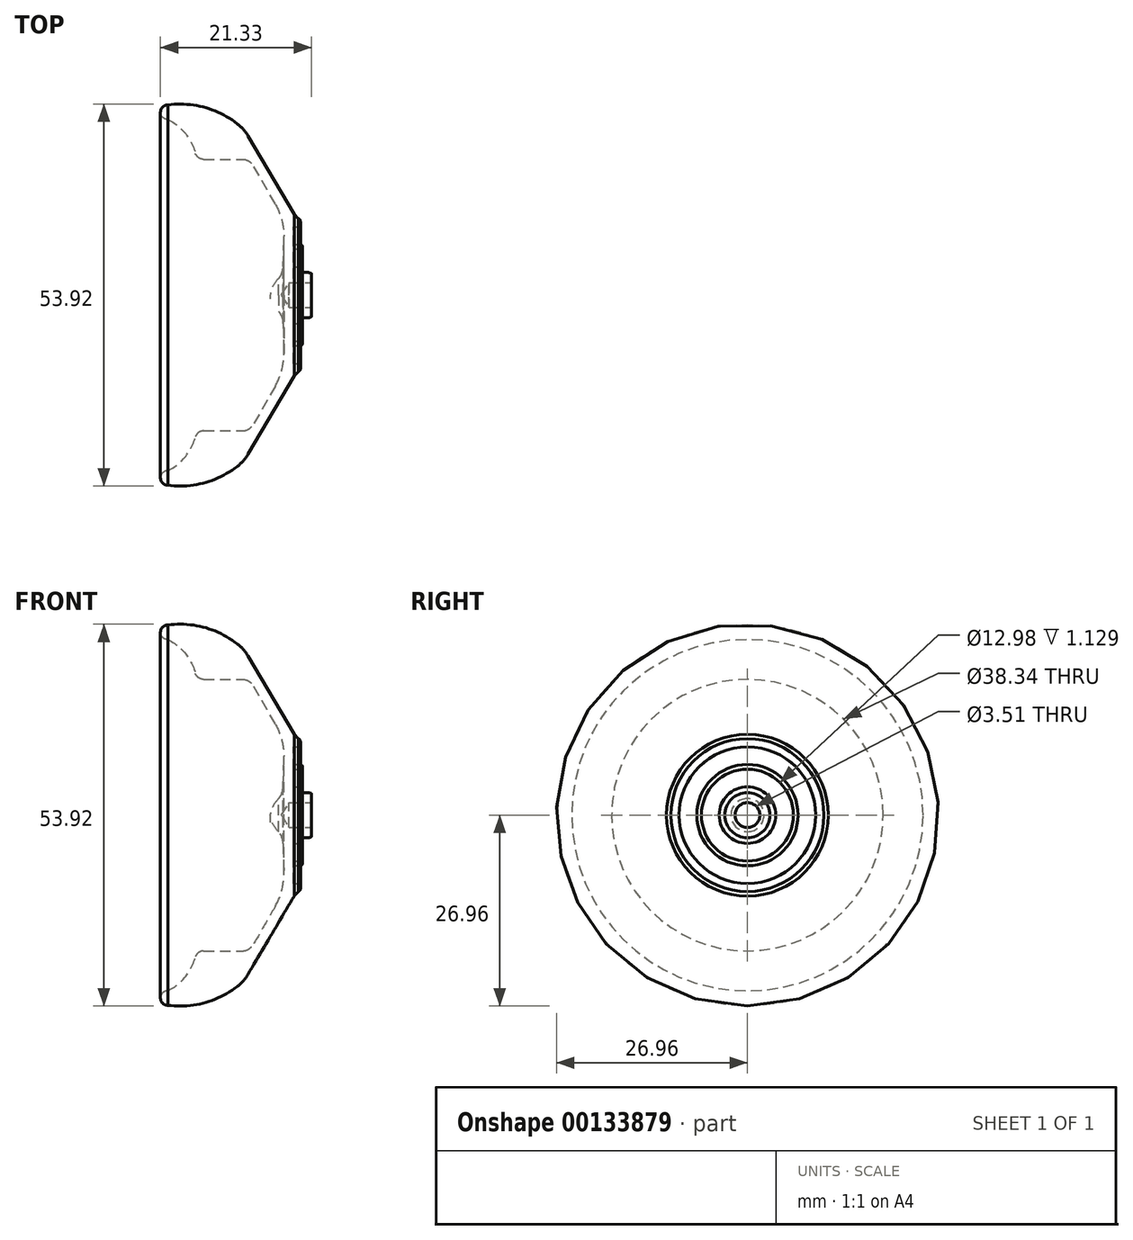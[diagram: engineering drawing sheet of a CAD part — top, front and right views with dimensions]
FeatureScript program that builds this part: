
annotation { "Feature Type Name" : "Feature", "Feature Type Description" : "" }
export const myFeature = defineFeature(function(context is Context, id is Id, definition is map)
    precondition{}
    {
        {
            var Q0;
            Q0=qCreatedBy(makeId("Front.planeOp"),FACE);
            var sketch = newSketch(context, id + "F0", { "sketchPlane" : qUnion([Q0])});
            skLineSegment(sketch, "E0", {"start": v(2.38, 10.8) * mm, "end": v(1.8, 11.42) * mm});
            skLineSegment(sketch, "E1", {"start": v(4.25, 1.75) * mm, "end": v(1.05, 1.75) * mm});
            skLineSegment(sketch, "E2", {"start": v(1.67, 7.15) * mm, "end": v(1.67, 9.65) * mm});
            skLineSegment(sketch, "E3", {"start": v(1.67, 9.65) * mm, "end": v(2.42, 9.65) * mm});
            skLineSegment(sketch, "E4", {"start": v(2.93, 6.62) * mm, "end": v(2.93, 6.9) * mm});
            skArc(sketch, "E5", {"start": v(2.93, 6.9) * mm, "mid": v(2.85, 7.08) * mm, "end": v(2.67, 7.15) * mm});
            skLineSegment(sketch, "E6", {"start": v(1.67, 6.5) * mm, "end": v(2.8, 6.5) * mm});
            skLineSegment(sketch, "E7", {"start": v(1.67, 4) * mm, "end": v(1.67, 6.5) * mm});
            skLineSegment(sketch, "E8", {"start": v(1.67, 4) * mm, "end": v(2.37, 4) * mm});
            skLineSegment(sketch, "E9", {"start": v(4.25, 1.75) * mm, "end": v(4.25, 2.97) * mm});
            skLineSegment(sketch, "E10", {"start": v(2.37, 3.19) * mm, "end": v(2.37, 4) * mm});
            skLineSegment(sketch, "E11", {"start": v(4.16, 3.09) * mm, "end": v(3.88, 3.18) * mm});
            skLineSegment(sketch, "E12", {"start": v(2.37, 3.19) * mm, "end": v(3.84, 3.19) * mm});
            skLineSegment(sketch, "E13", {"start": v(1.67, 7.15) * mm, "end": v(2.67, 7.15) * mm});
            skArc(sketch, "E14", {"start": v(3.88, 3.18) * mm, "mid": v(3.86, 3.18) * mm, "end": v(3.84, 3.19) * mm});
            skLineSegment(sketch, "E15", {"start": v(0, 0) * mm, "end": v(-1.6, 0) * mm});
            skArc(sketch, "E16", {"start": v(-0.4, 2.34) * mm, "mid": v(0.05, 3.12) * mm, "end": v(0.21, 4.02) * mm});
            skArc(sketch, "E17", {"start": v(-0.4, 2.34) * mm, "mid": v(-1.2, 1.27) * mm, "end": v(-1.6, 0) * mm});
            skArc(sketch, "E18", {"start": v(-6.25, 24.2) * mm, "mid": v(-10.88, 26.5) * mm, "end": v(-16.05, 26.84) * mm});
            skLineSegment(sketch, "E19", {"start": v(-4.73, 22.47) * mm, "end": v(1.8, 11.42) * mm});
            skLineSegment(sketch, "E20.1", {"start": v(-3.96, 18.25) * mm, "end": v(-0.87, 12.85) * mm});
            skLineSegment(sketch, "E21", {"start": v(0.33, 8.02) * mm, "end": v(0.21, 4.02) * mm});
            skLineSegment(sketch, "E22", {"start": v(-5.55, 19.17) * mm, "end": v(-10.99, 19.17) * mm});
            skPoint(sketch, "E23.second.point", {"position": v(-16.05, 24.8) * mm});
            skArc(sketch, "E24", {"start": v(-12.17, 20.08) * mm, "mid": v(-13.6, 22.86) * mm, "end": v(-16.05, 24.8) * mm});
            skPoint(sketch, "E25.visualSharp", {"position": v(-11.99, 19.17) * mm});
            skArc(sketch, "E25.filletArc", {"start": v(-12.17, 20.08) * mm, "mid": v(-11.73, 19.42) * mm, "end": v(-10.99, 19.17) * mm});
            skPoint(sketch, "E26.visualSharp", {"position": v(-4.49, 19.17) * mm});
            skArc(sketch, "E26.filletArc", {"start": v(-3.96, 18.25) * mm, "mid": v(-4.63, 18.92) * mm, "end": v(-5.55, 19.17) * mm});
            skArc(sketch, "E27.filletArc", {"start": v(0.33, 8.02) * mm, "mid": v(0.07, 10.52) * mm, "end": v(-0.87, 12.85) * mm});
            skLineSegment(sketch, "E28", {"start": v(-23.85, 0) * mm, "end": v(-23.85, 27) * mm});
            skPoint(sketch, "E29.third.point", {"position": v(-16.92, 25.62) * mm});
            skArc(sketch, "E30", {"start": v(-16.05, 26.84) * mm, "mid": v(-17.08, 25.82) * mm, "end": v(-16.05, 24.8) * mm});
            skArc(sketch, "E31", {"start": v(2.42, 9.65) * mm, "mid": v(2.6, 9.73) * mm, "end": v(2.67, 9.9) * mm});
            skLineSegment(sketch, "E32", {"start": v(1.05, 1.75) * mm, "end": v(0, 0) * mm});
            skArc(sketch, "E33", {"start": v(2.8, 6.5) * mm, "mid": v(2.9, 6.53) * mm, "end": v(2.93, 6.62) * mm});
            skArc(sketch, "E34", {"start": v(4.25, 2.97) * mm, "mid": v(4.22, 3.04) * mm, "end": v(4.16, 3.09) * mm});
            skLineSegment(sketch, "E35", {"start": v(4.75, 1) * mm, "end": v(4.75, 2.5) * mm});
            skLineSegment(sketch, "E36", {"start": v(-16.92, -6.74) * mm, "end": v(4.75, -6.74) * mm});
            skLineSegment(sketch, "E37", {"start": v(-16.92, -3.56) * mm, "end": v(4.75, -3.56) * mm});
            skPoint(sketch, "E38.visualSharp", {"position": v(-5.23, 23.32) * mm});
            skArc(sketch, "E38.filletArc", {"start": v(-4.73, 22.47) * mm, "mid": v(-5.4, 23.4) * mm, "end": v(-6.25, 24.2) * mm});
            skLineSegment(sketch, "E39", {"start": v(2.67, 9.9) * mm, "end": v(2.67, 10.4) * mm});
            skArc(sketch, "E40", {"start": v(2.67, 10.4) * mm, "mid": v(2.6, 10.64) * mm, "end": v(2.38, 10.8) * mm});
            skSolve(sketch);
        }
        {
            var Q0;
            Q0=makeQuery(id+"F0.imprint","IMPRINT",FACE,{"disambiguationData":[TD([[makeQuery(id+"F0.imprint","IMPRINT",EDGE,{"derivedFrom":sQuery(id+"F0.wireOp",EDGE,"E0")}),1.0]])]});
            var Q1;
            Q1=sQuery(id+"F0.wireOp",EDGE,"E15");
            revolve(context, id + "F1", {"entities" : qUnion([Q0]), "axis" : qUnion([Q1]), "revolveType" : RevolveType.FULL});
        }
    });
